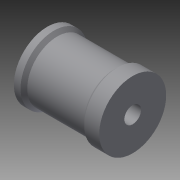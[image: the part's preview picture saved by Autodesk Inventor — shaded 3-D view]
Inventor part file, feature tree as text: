
AUTODESK INVENTOR PART (.ipt)
format: ipt  version: 2013 (Build 170138000, 138)  size: 98,304 bytes
history: native  units: mm
features: sketch x2, revolve x1, extrude x1
ambient origin geometry x8: Origin, YZ Plane, XZ Plane, XY Plane, X Axis, Y Axis, Z Axis, Center Point
bodies: Solid1 (feature_tree)
feature tree (4):
  revolve  "Revolution1"  [1 undecoded]
  extrude  "Extrusion1"  Depth=1.0mm
  sketch  "Sketch1"  dims[d0=25.5mm d1=9.0mm]
  sketch  "Sketch2"  dims[d2=17.0mm d3=1.0mm d4=2.0mm d5=90.0deg d6=5.0mm d8=10.0mm d9=0.0mm]
note: 1 required parameter value undecoded (feature->parameter linkage not recoverable at this tier; creation-order binding heuristic only, values carry confidence <= 0.55)
